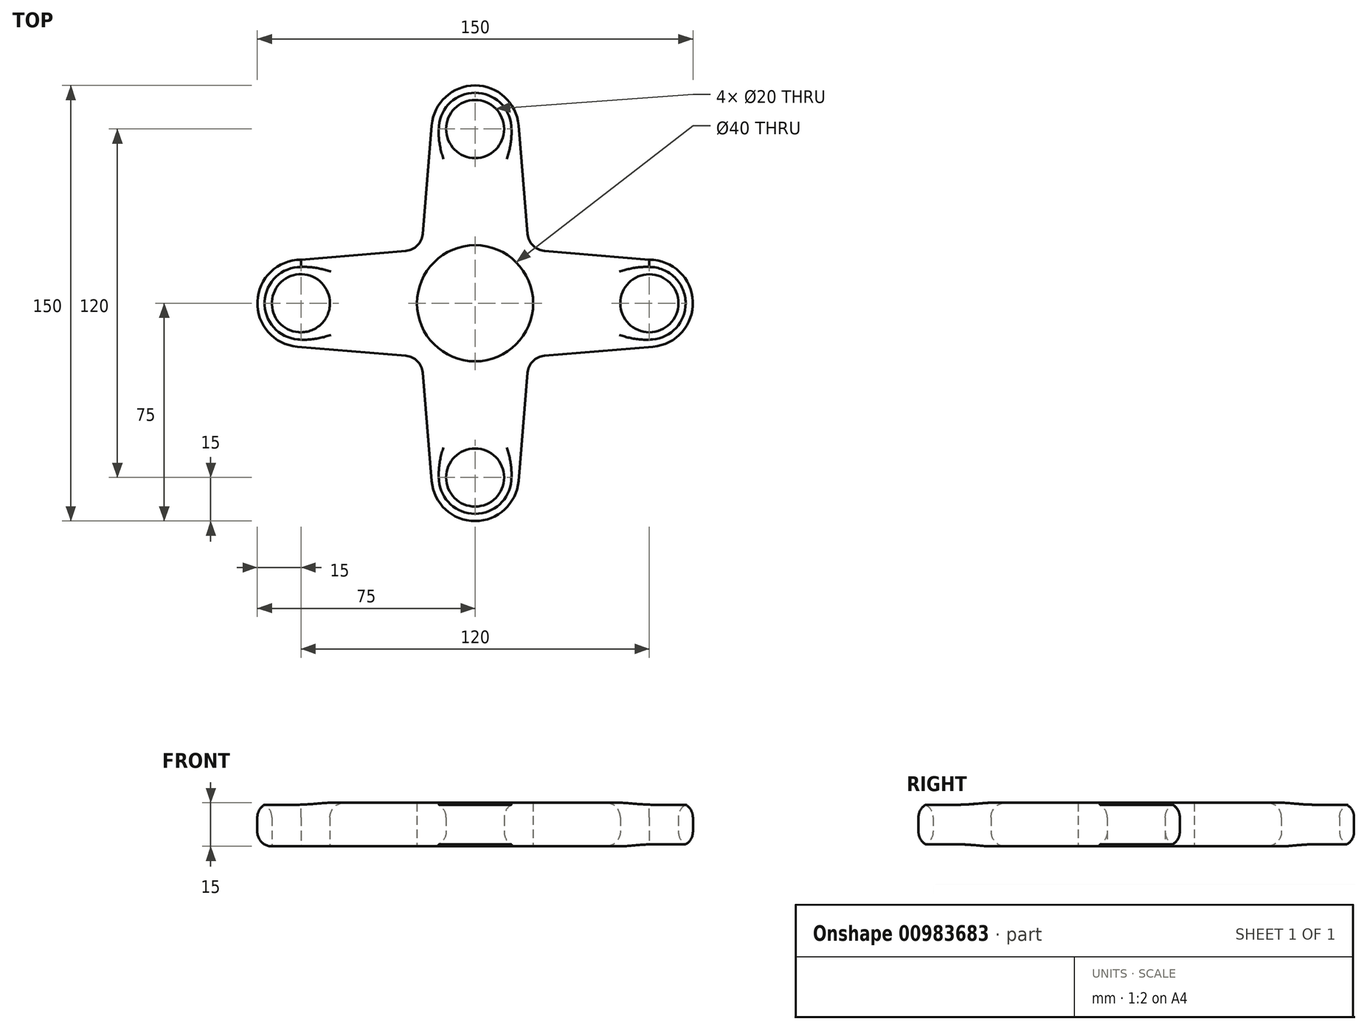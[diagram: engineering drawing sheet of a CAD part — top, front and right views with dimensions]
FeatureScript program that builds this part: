
annotation { "Feature Type Name" : "Feature", "Feature Type Description" : "" }
export const myFeature = defineFeature(function(context is Context, id is Id, definition is map)
    precondition{}
    {
        {
            var Q0;
            Q0=qCreatedBy(makeId("Top.planeOp"),FACE);
            var sketch = newSketch(context, id + "F0", { "sketchPlane" : qUnion([Q0])});
            skCircle(sketch, "E0", {"center": v(0, 0) * mm, "radius": 20 * mm});
            skCircle(sketch, "E1", {"center": v(0, 60) * mm, "radius": 15 * mm});
            skCircle(sketch, "E2", {"center": v(60, 0) * mm, "radius": 15 * mm});
            skCircle(sketch, "E3", {"center": v(0, -60) * mm, "radius": 15 * mm});
            skCircle(sketch, "E4", {"center": v(-60, 0) * mm, "radius": 15 * mm});
            skLineSegment(sketch, "E5", {"start": v(-18.08, 23.85) * mm, "end": v(-14.95, 61.25) * mm});
            skLineSegment(sketch, "E6", {"start": v(18.08, 23.85) * mm, "end": v(14.95, 61.25) * mm});
            skLineSegment(sketch, "E7", {"start": v(-23.87, 18.05) * mm, "end": v(-60, 15) * mm});
            skLineSegment(sketch, "E8", {"start": v(-23.87, -18.07) * mm, "end": v(-61.25, -14.95) * mm});
            skLineSegment(sketch, "E9", {"start": v(-18.07, -23.87) * mm, "end": v(-14.95, -61.25) * mm});
            skLineSegment(sketch, "E10", {"start": v(18.07, -23.87) * mm, "end": v(14.95, -61.25) * mm});
            skLineSegment(sketch, "E11", {"start": v(23.87, -18.07) * mm, "end": v(61.25, -14.95) * mm});
            skLineSegment(sketch, "E12", {"start": v(23.87, 18.05) * mm, "end": v(60, 15) * mm});
            skCircle(sketch, "E13", {"center": v(60, 0) * mm, "radius": 10 * mm});
            skCircle(sketch, "E14", {"center": v(0, -60) * mm, "radius": 10 * mm});
            skCircle(sketch, "E15", {"center": v(-60, 0) * mm, "radius": 10 * mm});
            skCircle(sketch, "E16", {"center": v(0, 60) * mm, "radius": 10 * mm});
            skArc(sketch, "E17.filletArc", {"start": v(23.87, -18.07) * mm, "mid": v(19.91, -19.91) * mm, "end": v(18.07, -23.87) * mm});
            skArc(sketch, "E18.filletArc", {"start": v(18.08, 23.85) * mm, "mid": v(19.91, 19.9) * mm, "end": v(23.87, 18.05) * mm});
            skPoint(sketch, "E19.newPointB", {"position": v(-19.93, 1.67) * mm});
            skArc(sketch, "E19.filletArc", {"start": v(-23.87, 18.05) * mm, "mid": v(-19.91, 19.9) * mm, "end": v(-18.08, 23.85) * mm});
            skPoint(sketch, "E20.newPointB", {"position": v(-19.93, -1.67) * mm});
            skArc(sketch, "E20.filletArc", {"start": v(-18.07, -23.87) * mm, "mid": v(-19.91, -19.91) * mm, "end": v(-23.87, -18.07) * mm});
            skSolve(sketch);
        }
        {
            var Q0;
            Q0 = qSketchRegion(id + "F0", true);
            extrude(context, id + "F1", {"entities" : qUnion([Q0]), "depth" : 15 * mm, "offsetDistance" : 25 * mm});
        }
        {
            var Q0;
            Q0=makeQuery(id+"F1.opExtrude","CAP_EDGE",EDGE,{"disambiguationData":[OSD([sQuery(id+"F0.wireOp",EDGE,"E8")])],"isStart":false});
            var Q1;
            Q1=makeQuery(id+"F1.opExtrude","CAP_EDGE",EDGE,{"disambiguationData":[OSD([sQuery(id+"F0.wireOp",EDGE,"E5")])],"isStart":false});
            var Q2;
            Q2=makeQuery(id+"F1.opExtrude","CAP_EDGE",EDGE,{"disambiguationData":[OSD([sQuery(id+"F0.wireOp",EDGE,"E11")])],"isStart":true});
            var Q3;
            Q3=makeQuery(id+"F1.opExtrude","CAP_EDGE",EDGE,{"disambiguationData":[OSD([sQuery(id+"F0.wireOp",EDGE,"E1")])],"isStart":true});
            var Q4;
            Q4=makeQuery(id+"F1.opExtrude","CAP_EDGE",EDGE,{"disambiguationData":[OSD([sQuery(id+"F0.wireOp",EDGE,"E13")])],"isStart":false});
            var Q5;
            Q5=makeQuery(id+"F1.opExtrude","CAP_EDGE",EDGE,{"disambiguationData":[OSD([sQuery(id+"F0.wireOp",EDGE,"E13")])],"isStart":true});
            var Q6;
            Q6=makeQuery(id+"F1.opExtrude","CAP_EDGE",EDGE,{"disambiguationData":[OSD([sQuery(id+"F0.wireOp",EDGE,"E16")])],"isStart":false});
            var Q7;
            Q7=makeQuery(id+"F1.opExtrude","CAP_EDGE",EDGE,{"disambiguationData":[OSD([sQuery(id+"F0.wireOp",EDGE,"E16")])],"isStart":true});
            var Q8;
            Q8=makeQuery(id+"F1.opExtrude","CAP_EDGE",EDGE,{"disambiguationData":[OSD([sQuery(id+"F0.wireOp",EDGE,"E15")])],"isStart":false});
            var Q9;
            Q9=makeQuery(id+"F1.opExtrude","CAP_EDGE",EDGE,{"disambiguationData":[OSD([sQuery(id+"F0.wireOp",EDGE,"E14")])],"isStart":true});
            var Q10;
            Q10=makeQuery(id+"F1.opExtrude","CAP_EDGE",EDGE,{"disambiguationData":[OSD([sQuery(id+"F0.wireOp",EDGE,"E14")])],"isStart":false});
            var Q11;
            Q11=makeQuery(id+"F1.opExtrude","CAP_EDGE",EDGE,{"disambiguationData":[OSD([sQuery(id+"F0.wireOp",EDGE,"E20.filletArc")])],"isStart":false});
            fillet(context, id + "F2", {"entities" : qUnion([Q0, Q1, Q2, Q3, Q4, Q5, Q6, Q7, Q8, Q9, Q10, Q11]), "radius" : 5 * mm, "tangentPropagation" : true, "allowEdgeOverflow" : false});
        }
    });
